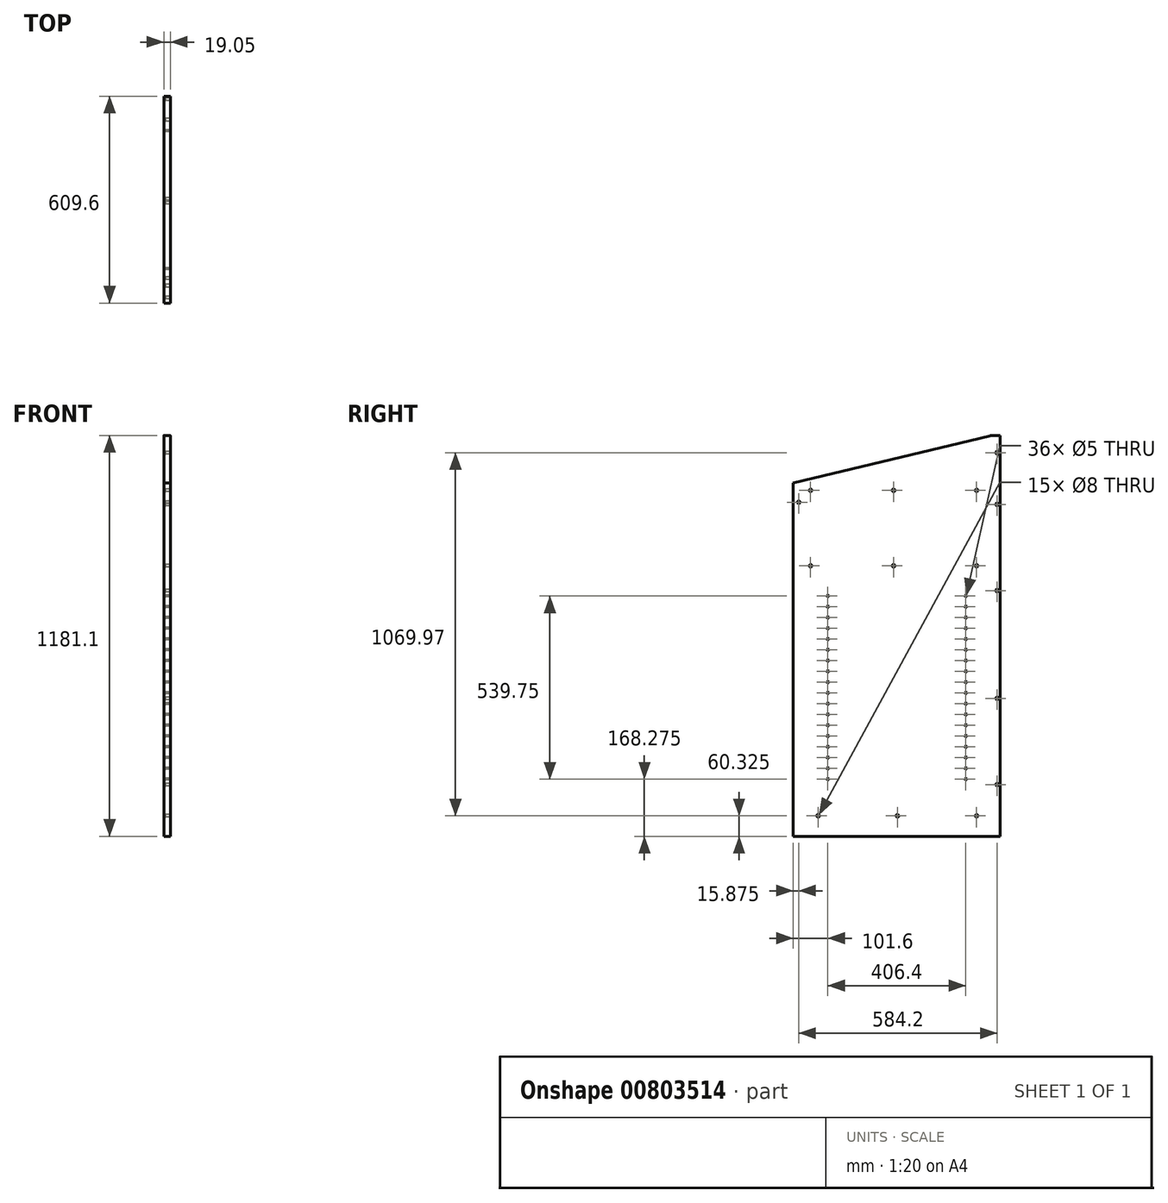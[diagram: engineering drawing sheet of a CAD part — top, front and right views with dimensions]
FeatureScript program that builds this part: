
annotation { "Feature Type Name" : "Feature", "Feature Type Description" : "" }
export const myFeature = defineFeature(function(context is Context, id is Id, definition is map)
    precondition{}
    {
        {
            var Q0;
            Q0=qCreatedBy(makeId("Right.planeOp"),FACE);
            var sketch = newSketch(context, id + "F0", { "sketchPlane" : qUnion([Q0])});
            skLineSegment(sketch, "E0.bottom", {"start": v(304.8, 590.55) * mm, "end": v(-304.8, 590.55) * mm});
            skLineSegment(sketch, "E0.top", {"start": v(304.8, -590.55) * mm, "end": v(-304.8, -590.55) * mm});
            skLineSegment(sketch, "E0.left", {"start": v(304.8, 590.55) * mm, "end": v(304.8, -590.55) * mm});
            skLineSegment(sketch, "E0.right", {"start": v(-304.8, 590.55) * mm, "end": v(-304.8, -590.55) * mm});
            skPoint(sketch, "E0.middle", {"position": v(0, 0) * mm});
            skLineSegment(sketch, "E1", {"start": v(304.8, 590.55) * mm, "end": v(285.39, 590.55) * mm});
            skLineSegment(sketch, "E2", {"start": v(-304.8, 590.55) * mm, "end": v(-304.8, 450.85) * mm});
            skLineSegment(sketch, "E3", {"start": v(-304.8, 450.85) * mm, "end": v(273.57, 589.16) * mm});
            skPoint(sketch, "E4.visualSharp", {"position": v(279.4, 590.55) * mm});
            skArc(sketch, "E4.filletArc", {"start": v(285.39, 590.55) * mm, "mid": v(279.44, 590.2) * mm, "end": v(273.57, 589.16) * mm});
            skLineSegment(sketch, "E5", {"start": v(-304.8, 450.85) * mm, "end": v(-304.8, 428.62) * mm});
            skSolve(sketch);
        }
        {
            var Q0;
            Q0=makeQuery(id+"F0.imprint","IMPRINT",FACE,{"disambiguationData":[TD([[makeQuery(id+"F0.imprint","IMPRINT",EDGE,{"derivedFrom":sQuery(id+"F0.wireOp",EDGE,"E0.top")}),-1.0]])]});
            extrude(context, id + "F1", {"entities" : qUnion([Q0]), "depth" : 19.05 * mm, "offsetDistance" : 25.4 * mm});
        }
        {
            var Q0;
            Q0=makeQuery(id+"F1.opExtrude","CAP_FACE",FACE,{"disambiguationData":[OSD([sQuery(id+"F0.wireOp",EDGE,"E0.top"),sQuery(id+"F0.wireOp",EDGE,"E0.left"),sQuery(id+"F0.wireOp",EDGE,"E0.right"),sQuery(id+"F0.wireOp",EDGE,"E1"),sQuery(id+"F0.wireOp",EDGE,"E3"),sQuery(id+"F0.wireOp",EDGE,"E4.filletArc"),sQuery(id+"F0.wireOp",EDGE,"E5")])],"isStart":false});
            var sketch = newSketch(context, id + "F2", { "sketchPlane" : qUnion([Q0])});
            skLineSegment(sketch, "E6.bottom", {"start": v(304.8, 590.55) * mm, "end": v(285.75, 590.55) * mm});
            skLineSegment(sketch, "E6.top", {"start": v(304.8, -590.55) * mm, "end": v(285.75, -590.55) * mm});
            skLineSegment(sketch, "E6.left", {"start": v(304.8, 590.55) * mm, "end": v(304.8, -590.55) * mm});
            skLineSegment(sketch, "E6.right", {"start": v(285.75, 590.55) * mm, "end": v(285.75, -590.55) * mm});
            skLineSegment(sketch, "E7", {"start": v(295.1, 590.55) * mm, "end": v(295.1, 539.75) * mm});
            skLineSegment(sketch, "E8", {"start": v(295.1, 590.55) * mm, "end": v(295.1, 387.35) * mm});
            skLineSegment(sketch, "E9", {"start": v(295.1, 590.55) * mm, "end": v(295.1, 133.35) * mm});
            skLineSegment(sketch, "E10", {"start": v(295.28, -590.55) * mm, "end": v(295.28, -438.15) * mm});
            skLineSegment(sketch, "E11", {"start": v(295.28, -590.55) * mm, "end": v(295.28, -184.15) * mm});
            skPoint(sketch, "E12", {"position": v(295.1, 539.75) * mm});
            skPoint(sketch, "E13", {"position": v(295.1, 387.35) * mm});
            skPoint(sketch, "E14", {"position": v(295.1, 133.35) * mm});
            skPoint(sketch, "E15", {"position": v(295.28, -184.15) * mm});
            skPoint(sketch, "E16", {"position": v(295.28, -438.15) * mm});
            skLineSegment(sketch, "E17", {"start": v(-304.8, 450.85) * mm, "end": v(-304.8, 438.15) * mm});
            skLineSegment(sketch, "E18.bottom", {"start": v(-304.8, 438.15) * mm, "end": v(285.75, 438.15) * mm});
            skLineSegment(sketch, "E18.top", {"start": v(-304.8, 419.1) * mm, "end": v(285.75, 419.1) * mm});
            skLineSegment(sketch, "E18.left", {"start": v(-304.8, 438.15) * mm, "end": v(-304.8, 419.1) * mm});
            skLineSegment(sketch, "E18.right", {"start": v(285.75, 438.15) * mm, "end": v(285.75, 419.1) * mm});
            skLineSegment(sketch, "E19", {"start": v(-304.8, -590.55) * mm, "end": v(-304.8, -539.75) * mm});
            skLineSegment(sketch, "E20", {"start": v(-304.8, -539.75) * mm, "end": v(-282.57, -539.75) * mm});
            skLineSegment(sketch, "E21.bottom", {"start": v(-282.57, -539.75) * mm, "end": v(285.75, -539.75) * mm});
            skLineSegment(sketch, "E21.top", {"start": v(-282.57, -511.18) * mm, "end": v(285.75, -511.18) * mm});
            skLineSegment(sketch, "E21.left", {"start": v(-282.57, -539.75) * mm, "end": v(-282.57, -511.18) * mm});
            skLineSegment(sketch, "E21.right", {"start": v(285.75, -539.75) * mm, "end": v(285.75, -511.18) * mm});
            skLineSegment(sketch, "E22", {"start": v(-304.8, 428.62) * mm, "end": v(-254, 428.62) * mm});
            skLineSegment(sketch, "E23", {"start": v(-9.52, 438.15) * mm, "end": v(-9.52, 428.62) * mm});
            skLineSegment(sketch, "E24", {"start": v(285.75, 428.62) * mm, "end": v(234.95, 428.62) * mm});
            skLineSegment(sketch, "E25", {"start": v(-304.8, 419.1) * mm, "end": v(-298.45, 419.1) * mm});
            skLineSegment(sketch, "E26.bottom", {"start": v(-298.45, 419.1) * mm, "end": v(-279.4, 419.1) * mm});
            skLineSegment(sketch, "E26.top", {"start": v(-298.45, 368.3) * mm, "end": v(-279.4, 368.3) * mm});
            skLineSegment(sketch, "E26.left", {"start": v(-298.45, 419.1) * mm, "end": v(-298.45, 368.3) * mm});
            skLineSegment(sketch, "E26.right", {"start": v(-279.4, 419.1) * mm, "end": v(-279.4, 368.3) * mm});
            skLineSegment(sketch, "E27", {"start": v(-288.92, 419.1) * mm, "end": v(-288.92, 393.7) * mm});
            skPoint(sketch, "E28", {"position": v(-288.92, 393.7) * mm});
            skPoint(sketch, "E29", {"position": v(-254, 428.62) * mm});
            skPoint(sketch, "E30", {"position": v(-9.52, 428.62) * mm});
            skPoint(sketch, "E31", {"position": v(234.95, 428.62) * mm});
            skLineSegment(sketch, "E32", {"start": v(-282.57, -539.75) * mm, "end": v(-282.57, -530.23) * mm});
            skLineSegment(sketch, "E33", {"start": v(-282.57, -530.23) * mm, "end": v(-231.77, -530.23) * mm});
            skLineSegment(sketch, "E34", {"start": v(-282.57, -530.23) * mm, "end": v(234.95, -530.23) * mm});
            skLineSegment(sketch, "E35", {"start": v(-282.57, -530.23) * mm, "end": v(-23.81, -530.23) * mm});
            skPoint(sketch, "E36", {"position": v(-231.77, -530.23) * mm});
            skPoint(sketch, "E37", {"position": v(-23.81, -530.23) * mm});
            skPoint(sketch, "E38", {"position": v(234.95, -530.23) * mm});
            skLineSegment(sketch, "E39", {"start": v(-304.8, 419.1) * mm, "end": v(-304.8, 215.9) * mm});
            skLineSegment(sketch, "E40.bottom", {"start": v(-304.8, 215.9) * mm, "end": v(285.75, 215.9) * mm});
            skLineSegment(sketch, "E40.top", {"start": v(-304.8, 196.85) * mm, "end": v(285.75, 196.85) * mm});
            skLineSegment(sketch, "E40.left", {"start": v(-304.8, 215.9) * mm, "end": v(-304.8, 196.85) * mm});
            skLineSegment(sketch, "E40.right", {"start": v(285.75, 215.9) * mm, "end": v(285.75, 196.85) * mm});
            skLineSegment(sketch, "E41", {"start": v(-304.8, 206.37) * mm, "end": v(-254, 206.37) * mm});
            skLineSegment(sketch, "E42", {"start": v(285.75, 206.37) * mm, "end": v(234.95, 206.37) * mm});
            skLineSegment(sketch, "E43", {"start": v(-9.52, 215.9) * mm, "end": v(-9.52, 206.37) * mm});
            skPoint(sketch, "E44", {"position": v(-9.52, 206.37) * mm});
            skPoint(sketch, "E45", {"position": v(-254, 206.37) * mm});
            skPoint(sketch, "E46", {"position": v(234.95, 206.37) * mm});
            skLineSegment(sketch, "E47", {"start": v(-282.57, -530.23) * mm, "end": v(1.6, -530.23) * mm});
            skPoint(sketch, "E48", {"position": v(1.6, -530.23) * mm});
            skSolve(sketch);
        }
        {
            var Q0;
            Q0=sQuery(id+"F2.wireOp",VERTEX,"E29");
            var Q1;
            Q1=sQuery(id+"F2.wireOp",VERTEX,"E28");
            var Q2;
            Q2=sQuery(id+"F2.wireOp",VERTEX,"E30");
            var Q3;
            Q3=sQuery(id+"F2.wireOp",VERTEX,"E31");
            var Q4;
            Q4=sQuery(id+"F2.wireOp",VERTEX,"E45");
            var Q5;
            Q5=sQuery(id+"F2.wireOp",VERTEX,"E44");
            var Q6;
            Q6=sQuery(id+"F2.wireOp",VERTEX,"E46");
            var Q7;
            Q7=sQuery(id+"F2.wireOp",VERTEX,"E12");
            var Q8;
            Q8=sQuery(id+"F2.wireOp",VERTEX,"E13");
            var Q9;
            Q9=sQuery(id+"F2.wireOp",VERTEX,"E14");
            var Q10;
            Q10=sQuery(id+"F2.wireOp",VERTEX,"E15");
            var Q11;
            Q11=sQuery(id+"F2.wireOp",VERTEX,"E16");
            var Q12;
            Q12=sQuery(id+"F2.wireOp",VERTEX,"E38");
            var Q13;
            Q13=sQuery(id+"F2.wireOp",VERTEX,"E36");
            var Q14;
            Q14=sQuery(id+"F2.wireOp",VERTEX,"E47.end");
            var Q15;
            Q15=makeQuery(id+"F1.opExtrude","SWEPT_BODY",BODY,{"disambiguationData":[OSD([sQuery(id+"F0.wireOp",EDGE,"E0.top"),sQuery(id+"F0.wireOp",EDGE,"E0.left"),sQuery(id+"F0.wireOp",EDGE,"E0.right"),sQuery(id+"F0.wireOp",EDGE,"E1"),sQuery(id+"F0.wireOp",EDGE,"E3"),sQuery(id+"F0.wireOp",EDGE,"E4.filletArc"),sQuery(id+"F0.wireOp",EDGE,"E5")])]});
            hole(context, id + "F3", {"style" : HoleStyle.SIMPLE, "endStyle" : HoleEndStyle.BLIND, "holeDiameter" : 8 * mm, "majorDiameter" : 6.35 * mm, "holeDepth" : 14.22 * mm, "isTappedThrough" : true, "tappedDepth" : 12.7 * mm, "tapClearance" : 3, "startFromSketch" : true, "locations" : qUnion([Q0, Q1, Q2, Q3, Q4, Q5, Q6, Q7, Q8, Q9, Q10, Q11, Q12, Q13, Q14]), "scope" : qUnion([Q15])});
        }
        {
            var Q0;
            Q0=makeQuery(id+"F1.opExtrude","CAP_FACE",FACE,{"disambiguationData":[OSD([sQuery(id+"F0.wireOp",EDGE,"E0.top"),sQuery(id+"F0.wireOp",EDGE,"E0.left"),sQuery(id+"F0.wireOp",EDGE,"E0.right"),sQuery(id+"F0.wireOp",EDGE,"E1"),sQuery(id+"F0.wireOp",EDGE,"E3"),sQuery(id+"F0.wireOp",EDGE,"E4.filletArc"),sQuery(id+"F0.wireOp",EDGE,"E5")])],"isStart":false});
            var sketch = newSketch(context, id + "F4", { "sketchPlane" : qUnion([Q0])});
            skLineSegment(sketch, "E49", {"start": v(0, -590.55) * mm, "end": v(0, -406.4) * mm});
            skLineSegment(sketch, "E50.bottom", {"start": v(203.2, -390.52) * mm, "end": v(-203.2, -390.52) * mm});
            skLineSegment(sketch, "E50.top", {"start": v(203.2, -422.27) * mm, "end": v(-203.2, -422.27) * mm});
            skLineSegment(sketch, "E50.left", {"start": v(203.2, -390.52) * mm, "end": v(203.2, -422.27) * mm});
            skLineSegment(sketch, "E50.right", {"start": v(-203.2, -390.52) * mm, "end": v(-203.2, -422.27) * mm});
            skPoint(sketch, "E50.middle", {"position": v(0, -406.4) * mm});
            skLineSegment(sketch, "E51.bottom", {"start": v(203.2, -358.77) * mm, "end": v(-203.2, -358.77) * mm});
            skLineSegment(sketch, "E51.top", {"start": v(203.2, -327.02) * mm, "end": v(-203.2, -327.02) * mm});
            skLineSegment(sketch, "E51.left", {"start": v(203.2, -358.77) * mm, "end": v(203.2, -327.02) * mm});
            skLineSegment(sketch, "E51.right", {"start": v(-203.2, -358.77) * mm, "end": v(-203.2, -327.02) * mm});
            skPoint(sketch, "E51.middle", {"position": v(0, -342.9) * mm});
            skLineSegment(sketch, "E52", {"start": v(0, -342.9) * mm, "end": v(0, -279.4) * mm});
            skLineSegment(sketch, "E53.bottom", {"start": v(203.2, -295.27) * mm, "end": v(-203.2, -295.27) * mm});
            skLineSegment(sketch, "E53.top", {"start": v(203.2, -263.52) * mm, "end": v(-203.2, -263.52) * mm});
            skLineSegment(sketch, "E53.left", {"start": v(203.2, -295.27) * mm, "end": v(203.2, -263.52) * mm});
            skLineSegment(sketch, "E53.right", {"start": v(-203.2, -295.27) * mm, "end": v(-203.2, -263.52) * mm});
            skPoint(sketch, "E53.middle", {"position": v(0, -279.4) * mm});
            skLineSegment(sketch, "E54", {"start": v(0, -279.4) * mm, "end": v(0, -215.9) * mm});
            skLineSegment(sketch, "E55.bottom", {"start": v(-203.2, -231.77) * mm, "end": v(203.2, -231.77) * mm});
            skLineSegment(sketch, "E55.top", {"start": v(-203.2, -200.02) * mm, "end": v(203.2, -200.02) * mm});
            skLineSegment(sketch, "E55.left", {"start": v(-203.2, -231.77) * mm, "end": v(-203.2, -200.02) * mm});
            skLineSegment(sketch, "E55.right", {"start": v(203.2, -231.77) * mm, "end": v(203.2, -200.02) * mm});
            skPoint(sketch, "E55.middle", {"position": v(0, -215.9) * mm});
            skLineSegment(sketch, "E56", {"start": v(0, -215.9) * mm, "end": v(0, -152.4) * mm});
            skLineSegment(sketch, "E57.bottom", {"start": v(-203.2, -168.27) * mm, "end": v(203.2, -168.27) * mm});
            skLineSegment(sketch, "E57.top", {"start": v(-203.2, -136.52) * mm, "end": v(203.2, -136.52) * mm});
            skLineSegment(sketch, "E57.left", {"start": v(-203.2, -168.27) * mm, "end": v(-203.2, -136.52) * mm});
            skLineSegment(sketch, "E57.right", {"start": v(203.2, -168.27) * mm, "end": v(203.2, -136.52) * mm});
            skPoint(sketch, "E57.middle", {"position": v(0, -152.4) * mm});
            skLineSegment(sketch, "E58", {"start": v(0, -152.4) * mm, "end": v(0, -88.9) * mm});
            skLineSegment(sketch, "E59.bottom", {"start": v(-203.2, -104.77) * mm, "end": v(203.2, -104.77) * mm});
            skLineSegment(sketch, "E59.top", {"start": v(-203.2, -73.02) * mm, "end": v(203.2, -73.02) * mm});
            skLineSegment(sketch, "E59.left", {"start": v(-203.2, -104.77) * mm, "end": v(-203.2, -73.02) * mm});
            skLineSegment(sketch, "E59.right", {"start": v(203.2, -104.77) * mm, "end": v(203.2, -73.02) * mm});
            skPoint(sketch, "E59.middle", {"position": v(0, -88.9) * mm});
            skLineSegment(sketch, "E60", {"start": v(0, -88.9) * mm, "end": v(0, -25.4) * mm});
            skLineSegment(sketch, "E61.bottom", {"start": v(-203.2, -41.27) * mm, "end": v(203.2, -41.27) * mm});
            skLineSegment(sketch, "E61.top", {"start": v(-203.2, -9.52) * mm, "end": v(203.2, -9.52) * mm});
            skLineSegment(sketch, "E61.left", {"start": v(-203.2, -41.27) * mm, "end": v(-203.2, -9.52) * mm});
            skLineSegment(sketch, "E61.right", {"start": v(203.2, -41.27) * mm, "end": v(203.2, -9.52) * mm});
            skPoint(sketch, "E61.middle", {"position": v(0, -25.4) * mm});
            skLineSegment(sketch, "E62", {"start": v(0, -25.4) * mm, "end": v(0, 38.1) * mm});
            skLineSegment(sketch, "E63.bottom", {"start": v(-203.2, 53.98) * mm, "end": v(203.2, 53.98) * mm});
            skLineSegment(sketch, "E63.top", {"start": v(-203.2, 22.23) * mm, "end": v(203.2, 22.23) * mm});
            skLineSegment(sketch, "E63.left", {"start": v(-203.2, 53.98) * mm, "end": v(-203.2, 22.23) * mm});
            skLineSegment(sketch, "E63.right", {"start": v(203.2, 53.98) * mm, "end": v(203.2, 22.23) * mm});
            skPoint(sketch, "E63.middle", {"position": v(0, 38.1) * mm});
            skLineSegment(sketch, "E64", {"start": v(0, 38.1) * mm, "end": v(0, 101.6) * mm});
            skLineSegment(sketch, "E65.bottom", {"start": v(-203.2, 85.73) * mm, "end": v(203.2, 85.73) * mm});
            skLineSegment(sketch, "E65.top", {"start": v(-203.2, 117.48) * mm, "end": v(203.2, 117.48) * mm});
            skLineSegment(sketch, "E65.left", {"start": v(-203.2, 85.73) * mm, "end": v(-203.2, 117.48) * mm});
            skLineSegment(sketch, "E65.right", {"start": v(203.2, 85.73) * mm, "end": v(203.2, 117.48) * mm});
            skPoint(sketch, "E65.middle", {"position": v(0, 101.6) * mm});
            skSolve(sketch);
        }
        {
            var Q0;
            Q0=sQuery(id+"F4.wireOp",VERTEX,"E65.top.start");
            var Q1;
            Q1=sQuery(id+"F4.wireOp",VERTEX,"E65.bottom.start");
            var Q2;
            Q2=sQuery(id+"F4.wireOp",VERTEX,"E63.bottom.start");
            var Q3;
            Q3=sQuery(id+"F4.wireOp",VERTEX,"E63.top.start");
            var Q4;
            Q4=sQuery(id+"F4.wireOp",VERTEX,"E61.top.start");
            var Q5;
            Q5=sQuery(id+"F4.wireOp",VERTEX,"E61.bottom.start");
            var Q6;
            Q6=sQuery(id+"F4.wireOp",VERTEX,"E59.top.start");
            var Q7;
            Q7=sQuery(id+"F4.wireOp",VERTEX,"E59.bottom.start");
            var Q8;
            Q8=sQuery(id+"F4.wireOp",VERTEX,"E57.top.start");
            var Q9;
            Q9=sQuery(id+"F4.wireOp",VERTEX,"E57.bottom.start");
            var Q10;
            Q10=sQuery(id+"F4.wireOp",VERTEX,"E55.top.start");
            var Q11;
            Q11=sQuery(id+"F4.wireOp",VERTEX,"E55.bottom.start");
            var Q12;
            Q12=sQuery(id+"F4.wireOp",VERTEX,"E53.top.end");
            var Q13;
            Q13=sQuery(id+"F4.wireOp",VERTEX,"E53.bottom.end");
            var Q14;
            Q14=sQuery(id+"F4.wireOp",VERTEX,"E51.top.end");
            var Q15;
            Q15=sQuery(id+"F4.wireOp",VERTEX,"E51.bottom.end");
            var Q16;
            Q16=sQuery(id+"F4.wireOp",VERTEX,"E50.bottom.end");
            var Q17;
            Q17=sQuery(id+"F4.wireOp",VERTEX,"E50.top.end");
            var Q18;
            Q18=sQuery(id+"F4.wireOp",VERTEX,"E50.top.start");
            var Q19;
            Q19=sQuery(id+"F4.wireOp",VERTEX,"E50.bottom.start");
            var Q20;
            Q20=sQuery(id+"F4.wireOp",VERTEX,"E51.bottom.start");
            var Q21;
            Q21=sQuery(id+"F4.wireOp",VERTEX,"E51.top.start");
            var Q22;
            Q22=sQuery(id+"F4.wireOp",VERTEX,"E53.bottom.start");
            var Q23;
            Q23=sQuery(id+"F4.wireOp",VERTEX,"E53.top.start");
            var Q24;
            Q24=sQuery(id+"F4.wireOp",VERTEX,"E55.bottom.end");
            var Q25;
            Q25=sQuery(id+"F4.wireOp",VERTEX,"E55.top.end");
            var Q26;
            Q26=sQuery(id+"F4.wireOp",VERTEX,"E57.bottom.end");
            var Q27;
            Q27=sQuery(id+"F4.wireOp",VERTEX,"E57.top.end");
            var Q28;
            Q28=sQuery(id+"F4.wireOp",VERTEX,"E59.bottom.end");
            var Q29;
            Q29=sQuery(id+"F4.wireOp",VERTEX,"E59.top.end");
            var Q30;
            Q30=sQuery(id+"F4.wireOp",VERTEX,"E61.bottom.end");
            var Q31;
            Q31=sQuery(id+"F4.wireOp",VERTEX,"E61.top.end");
            var Q32;
            Q32=sQuery(id+"F4.wireOp",VERTEX,"E63.top.end");
            var Q33;
            Q33=sQuery(id+"F4.wireOp",VERTEX,"E63.bottom.end");
            var Q34;
            Q34=sQuery(id+"F4.wireOp",VERTEX,"E65.bottom.end");
            var Q35;
            Q35=sQuery(id+"F4.wireOp",VERTEX,"E65.top.end");
            var Q36;
            Q36=makeQuery(id+"F1.opExtrude","SWEPT_BODY",BODY,{"disambiguationData":[OSD([sQuery(id+"F0.wireOp",EDGE,"E0.top"),sQuery(id+"F0.wireOp",EDGE,"E0.left"),sQuery(id+"F0.wireOp",EDGE,"E0.right"),sQuery(id+"F0.wireOp",EDGE,"E1"),sQuery(id+"F0.wireOp",EDGE,"E3"),sQuery(id+"F0.wireOp",EDGE,"E4.filletArc"),sQuery(id+"F0.wireOp",EDGE,"E5")])]});
            hole(context, id + "F5", {"style" : HoleStyle.SIMPLE, "endStyle" : HoleEndStyle.BLIND, "holeDiameter" : 5 * mm, "majorDiameter" : 6.35 * mm, "holeDepth" : 14.22 * mm, "isTappedThrough" : true, "tappedDepth" : 12.7 * mm, "tapClearance" : 3, "startFromSketch" : true, "locations" : qUnion([Q0, Q1, Q2, Q3, Q4, Q5, Q6, Q7, Q8, Q9, Q10, Q11, Q12, Q13, Q14, Q15, Q16, Q17, Q18, Q19, Q20, Q21, Q22, Q23, Q24, Q25, Q26, Q27, Q28, Q29, Q30, Q31, Q32, Q33, Q34, Q35]), "scope" : qUnion([Q36])});
        }
    });
